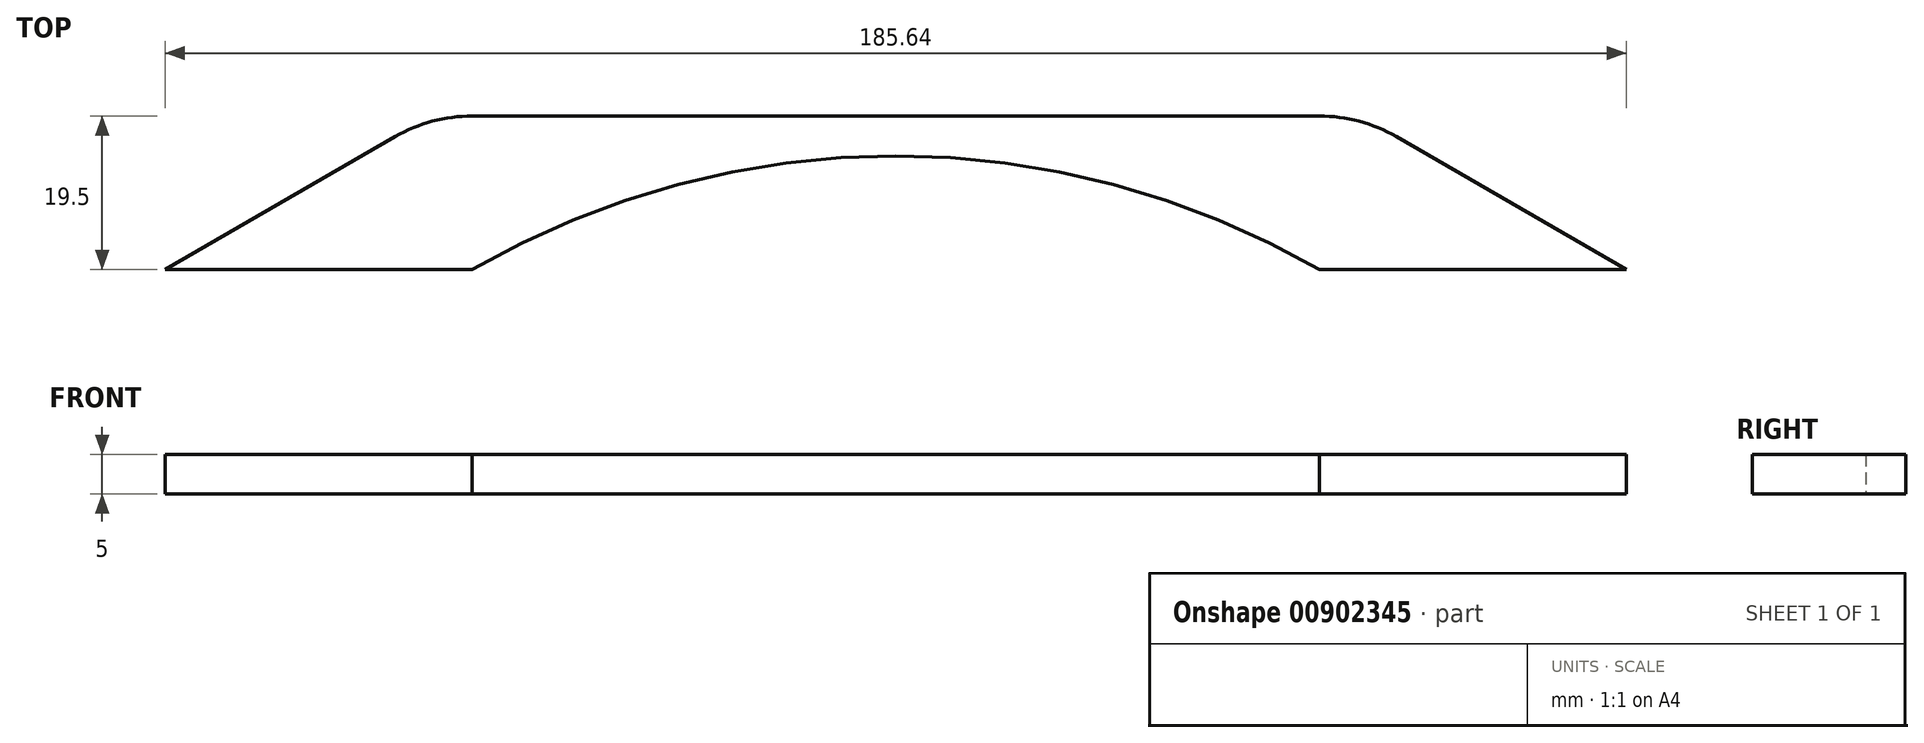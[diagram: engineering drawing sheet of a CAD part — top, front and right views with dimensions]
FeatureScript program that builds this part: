
annotation { "Feature Type Name" : "Feature", "Feature Type Description" : "" }
export const myFeature = defineFeature(function(context is Context, id is Id, definition is map)
    precondition{}
    {
        {
            var Q0;
            Q0=qCreatedBy(makeId("Top.planeOp"),FACE);
            var sketch = newSketch(context, id + "F0", { "sketchPlane" : qUnion([Q0])});
            skLineSegment(sketch, "E0.bottom", {"start": v(53.82, -9.75) * mm, "end": v(-53.82, -9.75) * mm});
            skLineSegment(sketch, "E0.top", {"start": v(53.82, 9.75) * mm, "end": v(-53.82, 9.75) * mm});
            skLineSegment(sketch, "E0.left", {"start": v(53.82, -9.75) * mm, "end": v(53.82, 9.75) * mm});
            skLineSegment(sketch, "E0.right", {"start": v(-53.82, -9.75) * mm, "end": v(-53.82, 9.75) * mm});
            skPoint(sketch, "E0.middle", {"position": v(0, 0) * mm});
            skLineSegment(sketch, "E1", {"start": v(-39.84, -9.75) * mm, "end": v(-9.49, -9.75) * mm});
            skLineSegment(sketch, "E2", {"start": v(-9.49, -9.75) * mm, "end": v(17.76, -9.75) * mm});
            skLineSegment(sketch, "E3", {"start": v(17.76, -9.75) * mm, "end": v(-95.75, -9.75) * mm});
            skLineSegment(sketch, "E4", {"start": v(-53.82, -9.75) * mm, "end": v(-63.57, 7.14) * mm});
            skArc(sketch, "E5", {"start": v(-53.82, 9.75) * mm, "mid": v(-58.86, 9.09) * mm, "end": v(-63.57, 7.14) * mm});
            skLineSegment(sketch, "E6", {"start": v(53.82, -9.75) * mm, "end": v(63.57, 7.14) * mm});
            skArc(sketch, "E7", {"start": v(53.82, 9.75) * mm, "mid": v(58.86, 9.09) * mm, "end": v(63.57, 7.14) * mm});
            skLineSegment(sketch, "E8", {"start": v(-63.57, 7.14) * mm, "end": v(-92.82, -9.75) * mm});
            skLineSegment(sketch, "E9", {"start": v(53.82, -9.75) * mm, "end": v(108.82, -9.75) * mm});
            skLineSegment(sketch, "E10", {"start": v(63.57, 7.14) * mm, "end": v(92.82, -9.75) * mm});
            skCircle(sketch, "E11", {"center": v(53.82, -9.75) * mm, "radius": 107.63 * mm});
            skCircle(sketch, "E12", {"center": v(-53.82, -9.75) * mm, "radius": 107.63 * mm});
            skCircle(sketch, "E13", {"center": v(0, -102.96) * mm, "radius": 107.63 * mm});
            skSolve(sketch);
        }
        {
            var Q0;
            {var subQ0=sQuery(id+"F0.wireOp",EDGE,"E4");Q0=makeQuery(id+"F0.imprint","IMPRINT",FACE,{"disambiguationData":[TD([[makeQuery(id+"F0.imprint","IMPRINT",EDGE,{"derivedFrom":subQ0}),1.0]])]});}
            var Q1;
            Q1=makeQuery(id+"F0.imprint","IMPRINT",FACE,{"disambiguationData":[TD([[makeQuery(id+"F0.imprint","IMPRINT",EDGE,{"derivedFrom":sQuery(id+"F0.wireOp",EDGE,"E0.right")}),1.0]])]});
            var Q2;
            {var subQ0=sQuery(id+"F0.wireOp",EDGE,"E0.right");Q2=makeQuery(id+"F0.imprint","IMPRINT",FACE,{"disambiguationData":[TD([[makeQuery(id+"F0.imprint","IMPRINT",EDGE,{"derivedFrom":subQ0}),-1.0]])]});}
            var Q3;
            {var subQ0=sQuery(id+"F0.wireOp",EDGE,"E12");var subQ1=sQuery(id+"F0.wireOp",EDGE,"E0.top");var subQ2=makeQuery(id+"F0.imprint","INTERSECT",VERTEX,{"derivedFrom":[subQ1,subQ0]});Q3=makeQuery(id+"F0.imprint","IMPRINT",FACE,{"disambiguationData":[TD([[makeQuery(id+"F0.imprint","IMPRINT",EDGE,{"disambiguationData":[TD([[subQ2,-1.0]])],"derivedFrom":subQ1}),1.0]])]});}
            var Q4;
            {var subQ0=sQuery(id+"F0.wireOp",EDGE,"E0.left");Q4=makeQuery(id+"F0.imprint","IMPRINT",FACE,{"disambiguationData":[TD([[makeQuery(id+"F0.imprint","IMPRINT",EDGE,{"derivedFrom":subQ0}),1.0]])]});}
            var Q5;
            Q5=makeQuery(id+"F0.imprint","IMPRINT",FACE,{"disambiguationData":[TD([[makeQuery(id+"F0.imprint","IMPRINT",EDGE,{"derivedFrom":sQuery(id+"F0.wireOp",EDGE,"E0.left")}),-1.0]])]});
            var Q6;
            {var subQ0=sQuery(id+"F0.wireOp",EDGE,"E6");Q6=makeQuery(id+"F0.imprint","IMPRINT",FACE,{"disambiguationData":[TD([[makeQuery(id+"F0.imprint","IMPRINT",EDGE,{"derivedFrom":subQ0}),-1.0]])]});}
            extrude(context, id + "F1", {"entities" : qUnion([Q0, Q1, Q2, Q3, Q4, Q5, Q6]), "depth" : 5 * mm, "offsetDistance" : 25 * mm});
        }
    });
